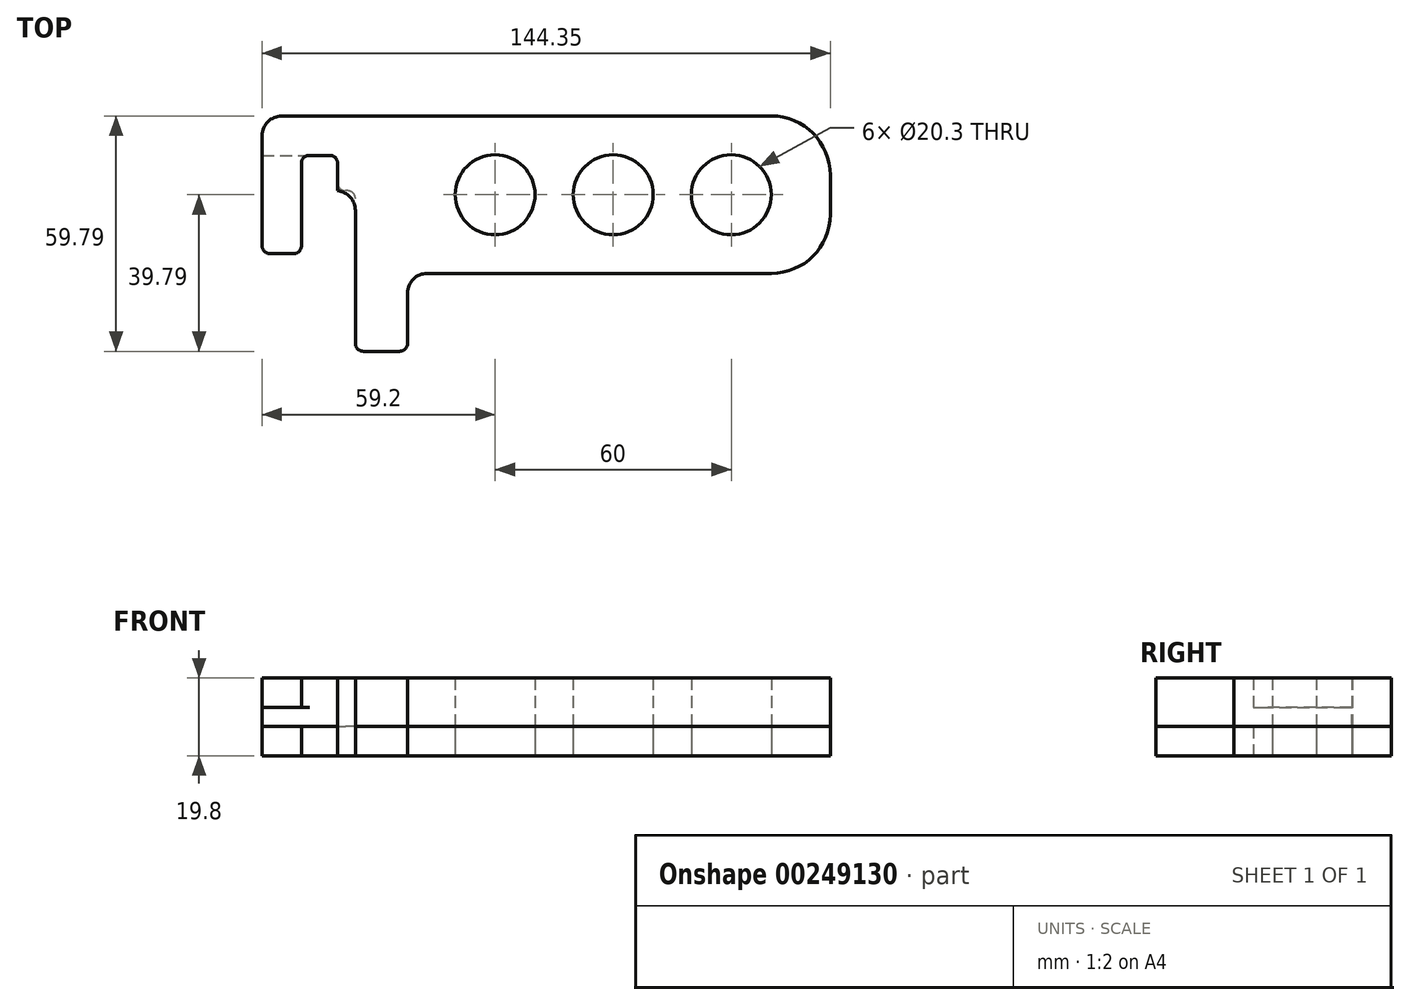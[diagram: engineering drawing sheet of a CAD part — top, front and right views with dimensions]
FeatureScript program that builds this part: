
annotation { "Feature Type Name" : "Feature", "Feature Type Description" : "" }
export const myFeature = defineFeature(function(context is Context, id is Id, definition is map)
    precondition{}
    {
        {
            var Q0;
            Q0=qCreatedBy(makeId("Top.planeOp"),FACE);
            var sketch = newSketch(context, id + "F0", { "sketchPlane" : qUnion([Q0])});
            skLineSegment(sketch, "E0", {"start": v(-59.2, -15) * mm, "end": v(-59.2, 20) * mm});
            skLineSegment(sketch, "E1", {"start": v(-59.2, 20) * mm, "end": v(85.15, 20) * mm});
            skLineSegment(sketch, "E2", {"start": v(85.15, 20) * mm, "end": v(85.15, -20) * mm});
            skLineSegment(sketch, "E3", {"start": v(85.15, -20) * mm, "end": v(-22.24, -20) * mm});
            skLineSegment(sketch, "E4", {"start": v(-35.5, -20) * mm, "end": v(-35.5, 1) * mm});
            skLineSegment(sketch, "E5", {"start": v(-40, 10) * mm, "end": v(-49.2, 10) * mm});
            skLineSegment(sketch, "E6", {"start": v(-49.2, 10) * mm, "end": v(-49.2, -15) * mm});
            skLineSegment(sketch, "E7", {"start": v(-49.2, -15) * mm, "end": v(-59.2, -15) * mm});
            skCircle(sketch, "E8", {"center": v(0, 0) * mm, "radius": 10.15 * mm});
            skCircle(sketch, "E9", {"center": v(60, 0) * mm, "radius": 10.15 * mm});
            skLineSegment(sketch, "E10", {"start": v(-35.5, 1) * mm, "end": v(-40, 1) * mm});
            skLineSegment(sketch, "E11", {"start": v(-40, 1) * mm, "end": v(-40, 10) * mm});
            skCircle(sketch, "E12", {"center": v(30, 0) * mm, "radius": 10.15 * mm});
            skLineSegment(sketch, "E13", {"start": v(-35.5, -20) * mm, "end": v(-35.5, -39.8) * mm});
            skLineSegment(sketch, "E14", {"start": v(-35.5, -39.8) * mm, "end": v(-22.24, -39.8) * mm});
            skLineSegment(sketch, "E15", {"start": v(-22.24, -39.8) * mm, "end": v(-22.24, -20) * mm});
            skSolve(sketch);
        }
        {
            var Q0;
            Q0=makeQuery(id+"F0.imprint","IMPRINT",FACE,{"disambiguationData":[TD([[makeQuery(id+"F0.imprint","IMPRINT",EDGE,{"derivedFrom":sQuery(id+"F0.wireOp",EDGE,"E0")}),-1.0]])]});
            var Q1;
            {var subQ3=sQuery(id+"F0.wireOp",EDGE,"E10");Q1=makeQuery(id+"F0.imprint","IMPRINT",FACE,{"disambiguationData":[TD([[makeQuery(id+"F0.imprint","IMPRINT",EDGE,{"derivedFrom":subQ3}),-1.0]])]});}
            var Q2;
            {var subQ0=sQuery(id+"F0.wireOp",EDGE,"E13");Q2=makeQuery(id+"F0.imprint","IMPRINT",FACE,{"disambiguationData":[TD([[makeQuery(id+"F0.imprint","IMPRINT",EDGE,{"derivedFrom":subQ0}),1.0]])]});}
            extrude(context, id + "F1", {"entities" : qUnion([Q0, Q1, Q2]), "depth" : 19.8 * mm});
        }
        {
            var Q0;
            Q0=makeQuery(id+"F1.opExtrude","SWEPT_EDGE",EDGE,{"disambiguationData":[OSD([sQuery(id+"F0.wireOp",EDGE,"E1"),sQuery(id+"F0.wireOp",EDGE,"E2")])]});
            var Q1;
            Q1=makeQuery(id+"F1.opExtrude","SWEPT_EDGE",EDGE,{"disambiguationData":[OSD([sQuery(id+"F0.wireOp",EDGE,"E2"),sQuery(id+"F0.wireOp",EDGE,"E3")])]});
            fillet(context, id + "F2", {"entities" : qUnion([Q0, Q1]), "radius" : 15 * mm, "tangentPropagation" : true, "allowEdgeOverflow" : false});
        }
        {
            var Q0;
            Q0=makeQuery(id+"F1.opExtrude","SWEPT_EDGE",EDGE,{"disambiguationData":[OSD([sQuery(id+"F0.wireOp",EDGE,"E3"),sQuery(id+"F0.wireOp",EDGE,"E4")])]});
            fillet(context, id + "F3", {"entities" : qUnion([Q0]), "radius" : 5 * mm, "tangentPropagation" : true, "allowEdgeOverflow" : false});
        }
        {
            var Q0;
            Q0=makeQuery(id+"F1.opExtrude","SWEPT_EDGE",EDGE,{"disambiguationData":[OSD([sQuery(id+"F0.wireOp",EDGE,"E0"),sQuery(id+"F0.wireOp",EDGE,"E1")])]});
            fillet(context, id + "F4", {"entities" : qUnion([Q0]), "radius" : 5 * mm, "tangentPropagation" : true, "allowEdgeOverflow" : false});
        }
        {
            var Q0;
            Q0=makeQuery(id+"F1.opExtrude","SWEPT_EDGE",EDGE,{"disambiguationData":[OSD([sQuery(id+"F0.wireOp",EDGE,"E6"),sQuery(id+"F0.wireOp",EDGE,"E7")])]});
            var Q1;
            Q1=makeQuery(id+"F1.opExtrude","SWEPT_EDGE",EDGE,{"disambiguationData":[OSD([sQuery(id+"F0.wireOp",EDGE,"E0"),sQuery(id+"F0.wireOp",EDGE,"E7")])]});
            fillet(context, id + "F5", {"entities" : qUnion([Q0, Q1]), "radius" : 2 * mm, "tangentPropagation" : true, "allowEdgeOverflow" : false});
        }
        {
            var Q0;
            Q0=makeQuery(id+"F1.opExtrude","SWEPT_EDGE",EDGE,{"disambiguationData":[OSD([sQuery(id+"F0.wireOp",EDGE,"E5"),sQuery(id+"F0.wireOp",EDGE,"E6")])]});
            var Q1;
            Q1=makeQuery(id+"F1.opExtrude","SWEPT_EDGE",EDGE,{"disambiguationData":[OSD([sQuery(id+"F0.wireOp",EDGE,"E4"),sQuery(id+"F0.wireOp",EDGE,"E5")])]});
            fillet(context, id + "F6", {"entities" : qUnion([Q0, Q1]), "radius" : 2 * mm, "tangentPropagation" : true, "allowEdgeOverflow" : false});
        }
        {
            var Q0;
            Q0=makeQuery(id+"F1.opExtrude","SWEPT_FACE",FACE,{"disambiguationData":[OSD([sQuery(id+"F0.wireOp",EDGE,"E7")])]});
            var sketch = newSketch(context, id + "F7", { "sketchPlane" : qUnion([Q0])});
            skLineSegment(sketch, "E16", {"start": v(-59.2, 9.9) * mm, "end": v(-47.2, 9.9) * mm});
            skPoint(sketch, "E16.startSnap0", {"position": v(-51.2, 9.9) * mm});
            skLineSegment(sketch, "E17.bottom", {"start": v(-59.2, 7.5) * mm, "end": v(-47.2, 7.5) * mm});
            skLineSegment(sketch, "E17.top", {"start": v(-59.2, 12.3) * mm, "end": v(-47.2, 12.3) * mm});
            skLineSegment(sketch, "E17.left", {"start": v(-59.2, 7.5) * mm, "end": v(-59.2, 12.3) * mm});
            skLineSegment(sketch, "E17.right", {"start": v(-47.2, 7.5) * mm, "end": v(-47.2, 12.3) * mm});
            skLineSegment(sketch, "E18.0", {"start": v(-59.2, 0) * mm, "end": v(-59.2, 19.8) * mm});
            skLineSegment(sketch, "E19.0", {"start": v(-49.2, 19.8) * mm, "end": v(-49.2, 0) * mm});
            skLineSegment(sketch, "E20.0", {"start": v(-47.2, 19.8) * mm, "end": v(-47.2, 0) * mm});
            skSolve(sketch);
        }
        {
            var Q0;
            Q0 = qSketchRegion(id + "F7", true);
            var Q1;
            Q1=makeQuery(id+"F1.opExtrude","SWEPT_BODY",BODY,{"disambiguationData":[OSD([sQuery(id+"F0.wireOp",EDGE,"E0"),sQuery(id+"F0.wireOp",EDGE,"E1"),sQuery(id+"F0.wireOp",EDGE,"E2"),sQuery(id+"F0.wireOp",EDGE,"E3"),sQuery(id+"F0.wireOp",EDGE,"E4"),sQuery(id+"F0.wireOp",EDGE,"E5"),sQuery(id+"F0.wireOp",EDGE,"E6"),sQuery(id+"F0.wireOp",EDGE,"E7"),sQuery(id+"F0.wireOp",EDGE,"E8"),sQuery(id+"F0.wireOp",EDGE,"E9")])]});
            extrude(context, id + "F8", {"entities" : qUnion([Q0]), "operationType" : NewBodyOperationType.REMOVE, "oppositeDirection" : true, "endBoundEntityBody" : qUnion([Q1]), "depth" : 25 * mm});
        }
        {
            var Q0;
            Q0=makeQuery(id+"F1.opExtrude","SWEPT_EDGE",EDGE,{"disambiguationData":[OSD([sQuery(id+"F0.wireOp",EDGE,"E13"),sQuery(id+"F0.wireOp",EDGE,"E14")])]});
            var Q1;
            Q1=makeQuery(id+"F1.opExtrude","SWEPT_EDGE",EDGE,{"disambiguationData":[OSD([sQuery(id+"F0.wireOp",EDGE,"E14"),sQuery(id+"F0.wireOp",EDGE,"E15")])]});
            fillet(context, id + "F9", {"entities" : qUnion([Q0, Q1]), "radius" : 2 * mm, "tangentPropagation" : true, "allowEdgeOverflow" : false});
        }
        {
            var Q0;
            Q0 = qSketchRegion(id + "F0", true);
            extrude(context, id + "F10", {"entities" : qUnion([Q0]), "depth" : 7.5 * mm, "offsetDistance" : 25 * mm});
        }
        {
            var Q0;
            Q0=makeQuery(id+"F10.opExtrude","SWEPT_EDGE",EDGE,{"disambiguationData":[OSD([sQuery(id+"F0.wireOp",EDGE,"E1"),sQuery(id+"F0.wireOp",EDGE,"E2")])]});
            var Q1;
            Q1=makeQuery(id+"F10.opExtrude","SWEPT_EDGE",EDGE,{"disambiguationData":[OSD([sQuery(id+"F0.wireOp",EDGE,"E2"),sQuery(id+"F0.wireOp",EDGE,"E3")])]});
            fillet(context, id + "F11", {"entities" : qUnion([Q0, Q1]), "radius" : 15 * mm, "tangentPropagation" : true, "allowEdgeOverflow" : false});
        }
        {
            var Q0;
            Q0=makeQuery(id+"F10.opExtrude","SWEPT_EDGE",EDGE,{"disambiguationData":[OSD([sQuery(id+"F0.wireOp",EDGE,"E0"),sQuery(id+"F0.wireOp",EDGE,"E7")])]});
            var Q1;
            Q1=makeQuery(id+"F10.opExtrude","SWEPT_EDGE",EDGE,{"disambiguationData":[OSD([sQuery(id+"F0.wireOp",EDGE,"E6"),sQuery(id+"F0.wireOp",EDGE,"E7")])]});
            var Q2;
            Q2=makeQuery(id+"F10.opExtrude","SWEPT_EDGE",EDGE,{"disambiguationData":[OSD([sQuery(id+"F0.wireOp",EDGE,"E13"),sQuery(id+"F0.wireOp",EDGE,"E14")])]});
            var Q3;
            Q3=makeQuery(id+"F10.opExtrude","SWEPT_EDGE",EDGE,{"disambiguationData":[OSD([sQuery(id+"F0.wireOp",EDGE,"E14"),sQuery(id+"F0.wireOp",EDGE,"E15")])]});
            var Q4;
            Q4=makeQuery(id+"F10.opExtrude","SWEPT_EDGE",EDGE,{"disambiguationData":[OSD([sQuery(id+"F0.wireOp",EDGE,"E5"),sQuery(id+"F0.wireOp",EDGE,"E11")])]});
            var Q5;
            Q5=makeQuery(id+"F10.opExtrude","SWEPT_EDGE",EDGE,{"disambiguationData":[OSD([sQuery(id+"F0.wireOp",EDGE,"E10"),sQuery(id+"F0.wireOp",EDGE,"E11")])]});
            var Q6;
            Q6=makeQuery(id+"F10.opExtrude","SWEPT_EDGE",EDGE,{"disambiguationData":[OSD([sQuery(id+"F0.wireOp",EDGE,"E4"),sQuery(id+"F0.wireOp",EDGE,"E10")])]});
            var Q7;
            Q7=makeQuery(id+"F10.opExtrude","SWEPT_EDGE",EDGE,{"disambiguationData":[OSD([sQuery(id+"F0.wireOp",EDGE,"E5"),sQuery(id+"F0.wireOp",EDGE,"E6")])]});
            fillet(context, id + "F12", {"entities" : qUnion([Q0, Q1, Q2, Q3, Q4, Q5, Q6, Q7]), "radius" : 2 * mm, "tangentPropagation" : true, "allowEdgeOverflow" : false});
        }
        {
            var Q0;
            Q0=makeQuery(id+"F10.opExtrude","SWEPT_EDGE",EDGE,{"disambiguationData":[OSD([sQuery(id+"F0.wireOp",EDGE,"E3"),sQuery(id+"F0.wireOp",EDGE,"E15")])]});
            var Q1;
            Q1=makeQuery(id+"F10.opExtrude","SWEPT_EDGE",EDGE,{"disambiguationData":[OSD([sQuery(id+"F0.wireOp",EDGE,"E0"),sQuery(id+"F0.wireOp",EDGE,"E1")])]});
            fillet(context, id + "F13", {"entities" : qUnion([Q0, Q1]), "radius" : 5 * mm, "tangentPropagation" : true, "allowEdgeOverflow" : false});
        }
    });
